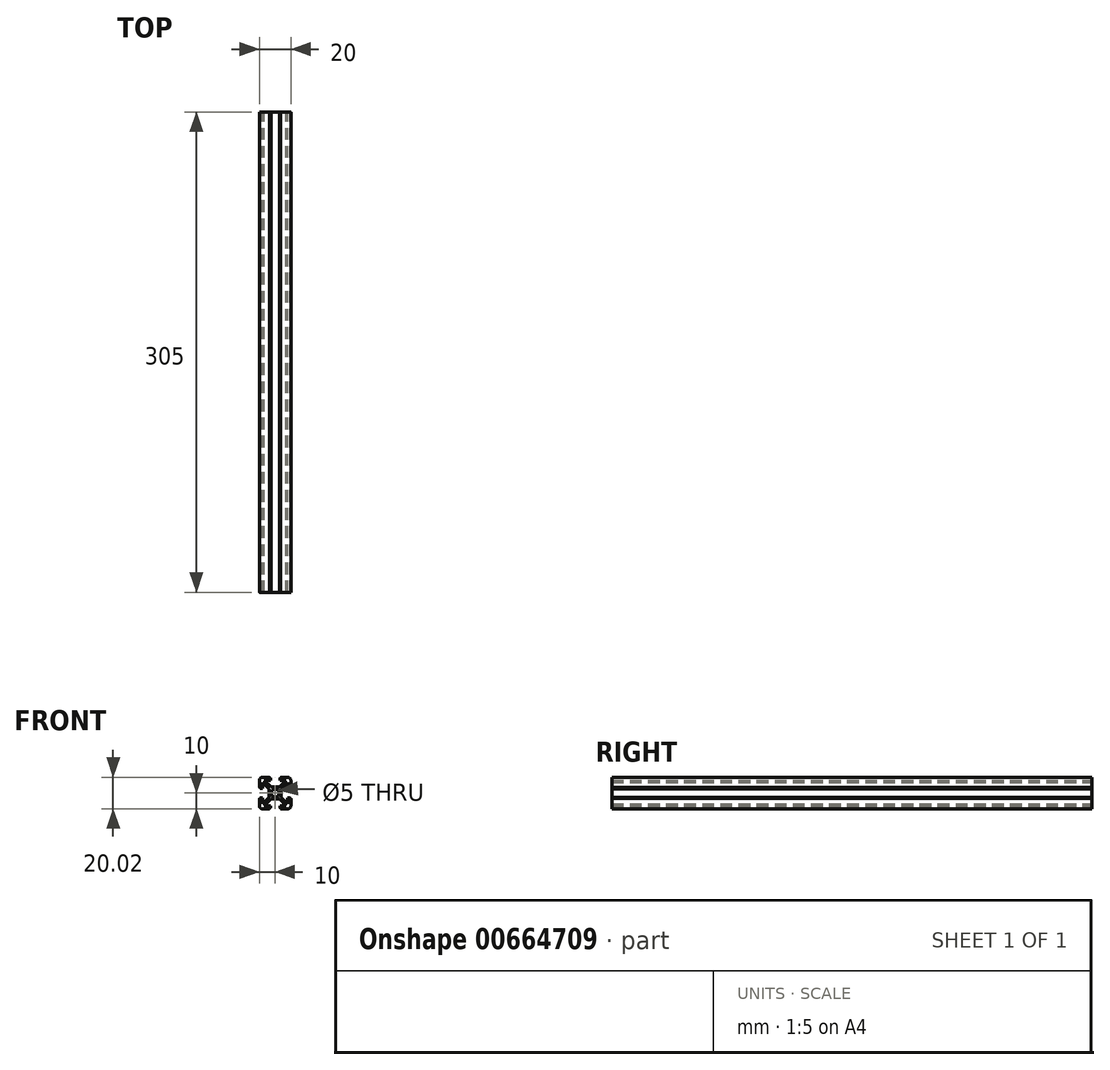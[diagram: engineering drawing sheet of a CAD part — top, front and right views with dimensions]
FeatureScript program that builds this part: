
annotation { "Feature Type Name" : "Feature", "Feature Type Description" : "" }
export const myFeature = defineFeature(function(context is Context, id is Id, definition is map)
    precondition{}
    {
        {
            var Q0;
            Q0=qCreatedBy(makeId("Front.planeOp"),FACE);
            var sketch = newSketch(context, id + "F0", { "sketchPlane" : qUnion([Q0])});
            skPoint(sketch, "E0.middle", {"position": v(0, 0) * mm});
            skPoint(sketch, "E1.visualSharp", {"position": v(-10, 10) * mm});
            skArc(sketch, "E1.filletArc", {"start": v(-8, 10) * mm, "mid": v(-9.41, 9.41) * mm, "end": v(-10, 8) * mm});
            skPoint(sketch, "E2.visualSharp", {"position": v(10, 10) * mm});
            skArc(sketch, "E2.filletArc", {"start": v(10, 8) * mm, "mid": v(9.41, 9.41) * mm, "end": v(8, 10) * mm});
            skPoint(sketch, "E3.visualSharp", {"position": v(10, -10) * mm});
            skArc(sketch, "E3.filletArc", {"start": v(8, -10) * mm, "mid": v(9.41, -9.41) * mm, "end": v(10, -8) * mm});
            skArc(sketch, "E4.filletArc", {"start": v(-10, -8) * mm, "mid": v(-9.41, -9.41) * mm, "end": v(-8, -10) * mm});
            skLineSegment(sketch, "E5", {"start": v(-8, 10) * mm, "end": v(-3.5, 10) * mm});
            skLineSegment(sketch, "E6", {"start": v(-3.5, 10) * mm, "end": v(-3.5, 9.5) * mm});
            skLineSegment(sketch, "E7", {"start": v(3.02, 9.5) * mm, "end": v(3.5, 9.5) * mm});
            skLineSegment(sketch, "E8", {"start": v(3.5, 10.02) * mm, "end": v(8, 10) * mm});
            skLineSegment(sketch, "E9", {"start": v(10, 8) * mm, "end": v(10, 3.5) * mm});
            skLineSegment(sketch, "E10", {"start": v(10, 3.5) * mm, "end": v(9.5, 3.5) * mm});
            skLineSegment(sketch, "E11", {"start": v(9.5, 3.5) * mm, "end": v(9.5, 3) * mm});
            skLineSegment(sketch, "E12", {"start": v(3.83, 2.75) * mm, "end": v(3.83, -2.77) * mm});
            skLineSegment(sketch, "E13", {"start": v(9.53, -2.98) * mm, "end": v(9.54, -3.46) * mm});
            skLineSegment(sketch, "E14", {"start": v(10, -3.46) * mm, "end": v(10, -8) * mm});
            skLineSegment(sketch, "E15", {"start": v(8, -10) * mm, "end": v(3.5, -10) * mm});
            skLineSegment(sketch, "E16", {"start": v(3.5, -10) * mm, "end": v(3.5, -9.5) * mm});
            skLineSegment(sketch, "E17", {"start": v(2.74, -3.8) * mm, "end": v(-2.74, -3.8) * mm});
            skLineSegment(sketch, "E18", {"start": v(-3, -9.5) * mm, "end": v(-3.5, -9.5) * mm});
            skLineSegment(sketch, "E19", {"start": v(-3.5, -9.5) * mm, "end": v(-3.5, -10) * mm});
            skLineSegment(sketch, "E20", {"start": v(-3.5, -10) * mm, "end": v(-8, -10) * mm});
            skLineSegment(sketch, "E21", {"start": v(-10, -8) * mm, "end": v(-10, -3.5) * mm});
            skLineSegment(sketch, "E22", {"start": v(-3.8, -2.74) * mm, "end": v(-3.8, 2.74) * mm});
            skLineSegment(sketch, "E23", {"start": v(-10, 3.51) * mm, "end": v(-10, 8) * mm});
            skLineSegment(sketch, "E24", {"start": v(-3, -9.5) * mm, "end": v(-3, -8) * mm});
            skLineSegment(sketch, "E25", {"start": v(3.02, -9.5) * mm, "end": v(3.02, -8) * mm});
            skLineSegment(sketch, "E26", {"start": v(3.02, -8) * mm, "end": v(6.94, -8) * mm});
            skLineSegment(sketch, "E27", {"start": v(-3, 9.5) * mm, "end": v(-3, 8) * mm});
            skLineSegment(sketch, "E28", {"start": v(-3, 8) * mm, "end": v(-6.94, 8) * mm});
            skLineSegment(sketch, "E29", {"start": v(-6.94, 8) * mm, "end": v(-2.74, 3.8) * mm});
            skLineSegment(sketch, "E30", {"start": v(2.74, 3.8) * mm, "end": v(6.94, 8) * mm});
            skLineSegment(sketch, "E31", {"start": v(6.94, 8) * mm, "end": v(3.02, 8) * mm});
            skLineSegment(sketch, "E32", {"start": v(9.53, -2.98) * mm, "end": v(8, -2.98) * mm});
            skLineSegment(sketch, "E33", {"start": v(8, -2.98) * mm, "end": v(8, -6.94) * mm});
            skLineSegment(sketch, "E34", {"start": v(8, -6.94) * mm, "end": v(3.83, -2.77) * mm});
            skLineSegment(sketch, "E35", {"start": v(3.83, 2.75) * mm, "end": v(8, 6.94) * mm});
            skLineSegment(sketch, "E36", {"start": v(8, 6.94) * mm, "end": v(8, 3) * mm});
            skLineSegment(sketch, "E37", {"start": v(8, 3) * mm, "end": v(9.5, 3) * mm});
            skLineSegment(sketch, "E38", {"start": v(3.5, -9.5) * mm, "end": v(3.02, -9.5) * mm});
            skLineSegment(sketch, "E39", {"start": v(6.94, -8) * mm, "end": v(2.74, -3.8) * mm});
            skLineSegment(sketch, "E40", {"start": v(-2.74, -3.8) * mm, "end": v(-6.94, -8) * mm});
            skLineSegment(sketch, "E41", {"start": v(-6.94, -8) * mm, "end": v(-3, -8) * mm});
            skLineSegment(sketch, "E42", {"start": v(-3, -8) * mm, "end": v(-3, -9.5) * mm});
            skLineSegment(sketch, "E43", {"start": v(-9.5, 3.51) * mm, "end": v(-9.5, 3) * mm});
            skLineSegment(sketch, "E44", {"start": v(-9.5, 3) * mm, "end": v(-8, 3) * mm});
            skLineSegment(sketch, "E45", {"start": v(-8, 3) * mm, "end": v(-8, 6.92) * mm});
            skLineSegment(sketch, "E46", {"start": v(-8, 6.92) * mm, "end": v(-3.8, 2.74) * mm});
            skLineSegment(sketch, "E47", {"start": v(-3.8, -2.74) * mm, "end": v(-8, -6.94) * mm});
            skLineSegment(sketch, "E48", {"start": v(-8, -6.94) * mm, "end": v(-8, -3) * mm});
            skLineSegment(sketch, "E49", {"start": v(-8, -3) * mm, "end": v(-9.5, -3) * mm});
            skLineSegment(sketch, "E50", {"start": v(-9.5, -3) * mm, "end": v(-9.5, -3.5) * mm});
            skLineSegment(sketch, "E51", {"start": v(-9.5, -3.5) * mm, "end": v(-10, -3.5) * mm});
            skCircle(sketch, "E52", {"center": v(0, 0) * mm, "radius": 2.5 * mm});
            skLineSegment(sketch, "E53", {"start": v(3.5, 10.02) * mm, "end": v(3.5, 9.5) * mm});
            skLineSegment(sketch, "E54", {"start": v(-3.5, 9.5) * mm, "end": v(-3, 9.5) * mm});
            skLineSegment(sketch, "E55", {"start": v(3.02, 9.5) * mm, "end": v(3.02, 8) * mm});
            skLineSegment(sketch, "E56", {"start": v(-2.74, 3.8) * mm, "end": v(2.74, 3.8) * mm});
            skLineSegment(sketch, "E57", {"start": v(-10, 3.51) * mm, "end": v(-9.5, 3.51) * mm});
            skLineSegment(sketch, "E58", {"start": v(9.54, -3.46) * mm, "end": v(10, -3.46) * mm});
            skSolve(sketch);
        }
        {
            assignVariable(context, id + "F1", {"name" : "L", "anyValue" : 305 * mm});
        }
        {
            var Q0;
            Q0=qSketchRegion(id+"F0",true);
            extrude(context, id + "F2", {"entities" : qUnion([Q0]), "depth" : getVariable(context, 'L'), "offsetDistance" : 25 * mm});
        }
    });
